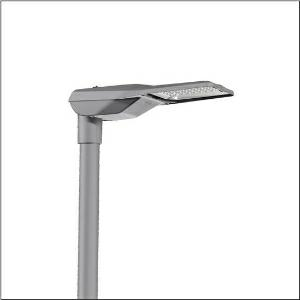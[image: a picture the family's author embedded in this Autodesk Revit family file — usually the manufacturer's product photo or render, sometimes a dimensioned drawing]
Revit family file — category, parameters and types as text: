
# Revit family: streetlight_sl_21_mini___p0_5a_5xe2v33s08jb_bee1
name_source: partatom
category: Lighting Fixtures
units: mm (PartAtom-declared; Revit-internal decimal feet)

## family parameters
Cut with Voids When Loaded = No
Host = Face
Light Source = No
Part Type = Normal
Room Calculation Point = No
Round Connector Dimension = Use Diameter
Shared = No

## types (1)
- --- (1 x LED, 12720 lm, 88.6 W, 3000K)
    Apparent Load = 89 VA
    CIE Flux Codes = 37 73 96 100 100
    Color Rendering = 70
    Color Temperature = 3000K
    Default Elevation = 1800 mm
    Description = Streetlight SL 21 mini, mast luminaire, primary light control with lens, of PMMA, primary optical cover: cover, of toughened safety glass, transparent, light distribution: P0.5a, light emission: direct distribution, primary light characteristic: asymmetric, installation type: post-top, side-entry, LED, High Power LED, rated luminous flux: 12.720lm, luminous efficacy: 144lm/W, light colour: 730, colour temperature: 3000K, control gear: D4i, control: pre-setting: logarithmic dimming characteristic, flexible luminous flux parameterisation, time-dependent luminous flux control, constant luminous flux control, overheat protection, mains connection: 220..240V, AC, 50/60Hz, start of lifetime: 89W, end of service life: 92W, reduction: 41W, luminaire housing, of diecast aluminium, powder-coated, SITECO metallic grey (DB 702S), corrosivity category C5 high according to DIN EN ISO 12944, multi-level sealing system, sealing non-destructively replaceable, inclination adjustable: 0°, 5°, 10°, 15°, please order mast flange separately, length: 628mm, width: 235mm, height: 110mm, mast flange for spigot size: 42mm (side-entry): 5XC10008XM4, 60/48mm (side-entry/post-top): 5XC10108XM2, 76/60mm (side-entry/post-top): 5XC10108XM1, mounting height: 4..8m, Smart Interface above, protection rating (complete): IP66, insulation class (complete): insulation class II (safety insulation), certification: CE, ENEC, ENEC+, VDE, impact resistance: IK10, permissible operating ambient temperature for outdoor applications: -40..+50°C, standard-compliant lighting for roads and squares, packaging unit: 1 piece

Light Distribution: P0.5a
    Height = 110 mm
    Lamp = 1 x LED
    Lamp Light Flux = 12720 lm
    Lamp Power = 88.6 W
    Lamp count = 1
    Length = 625 mm
    Luminous efficacy = 144 lm/W
    Manufacturer = Siteco
    ModVariant = No
    Model = 5XE2V33S08JB
    Number of Poles = 1
    OnlyDefault = Yes
    Power Factor = 1
    Product Name = Streetlight SL 21 mini | P0.5a
    Product group = mast luminaire | pylon top
    ProductGroupID = 6100
    Protection Class = Protection class II
    Protection Degree = IP 66
    RLX_Detail_Level = 1
    RLX_Emergency_Light_Flux = 0 lm
    RLX_Emergency_Type = 0
    RLX_Emergency_Type_DB = No
    RlxData = <blob elided: 25945 chars, md5=fe6a625e>
    Socket = socket
    Standby Power = 0 W
    System Light Flux = 12720 lm
    System Power = 89 W
    Type Comments = factory setting: luminous flux: 100 % | dim-lin: 254 | 915 mA
    Type Image = l_1003515.jpg
    URL = http://relux.com
    VarID = @adj_032735
    Voltage = 0 V
    Weight = 0.00 kg
    Width = 234 mm

## geometry (parser evidence)
native form markers: Blend x4, Sweep x13
no freeform markers — native parametric forms only
